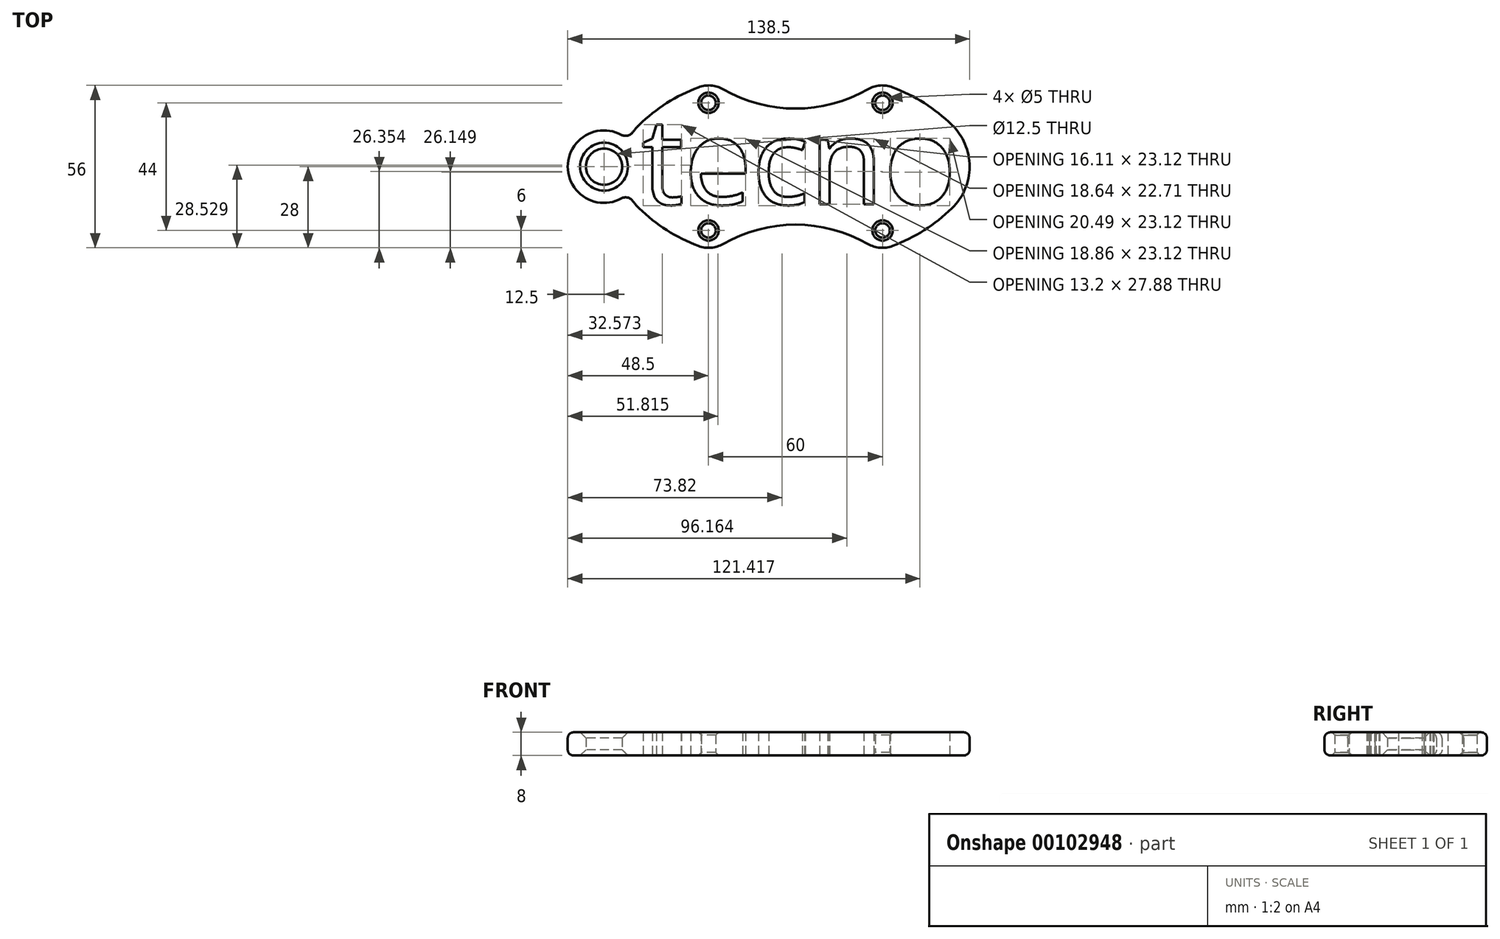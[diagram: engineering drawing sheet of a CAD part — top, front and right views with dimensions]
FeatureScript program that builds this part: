
annotation { "Feature Type Name" : "Feature", "Feature Type Description" : "" }
export const myFeature = defineFeature(function(context is Context, id is Id, definition is map)
    precondition{}
    {
        {
            var Q0;
            Q0=qCreatedBy(makeId("Top.planeOp"),FACE);
            var sketch = newSketch(context, id + "F0", { "sketchPlane" : qUnion([Q0])});
            skArc(sketch, "E0", {"start": v(-53.9, 14.37) * mm, "mid": v(-55.07, 13.14) * mm, "end": v(-56.13, 11.82) * mm});
            skArc(sketch, "E1.MirrorC", {"start": v(53.9, 14.37) * mm, "mid": v(60, 0) * mm, "end": v(53.9, -14.37) * mm});
            skArc(sketch, "E2", {"start": v(-53.9, -14.37) * mm, "mid": v(-44.35, -21.9) * mm, "end": v(-33.48, -27.35) * mm});
            skArc(sketch, "E3", {"start": v(24.94, -26.66) * mm, "mid": v(0, -20) * mm, "end": v(-24.94, -26.66) * mm});
            skArc(sketch, "E4", {"start": v(-33.48, -27.35) * mm, "mid": v(-29.13, -27.97) * mm, "end": v(-24.94, -26.66) * mm});
            skPoint(sketch, "E5.orphan", {"position": v(0, -30) * mm});
            skArc(sketch, "E6.MirrorCS", {"start": v(33.48, -27.35) * mm, "mid": v(29.13, -27.97) * mm, "end": v(24.94, -26.66) * mm});
            skArc(sketch, "E7.MirrorCS", {"start": v(53.9, -14.37) * mm, "mid": v(44.35, -21.9) * mm, "end": v(33.48, -27.35) * mm});
            skArc(sketch, "E8.MirrorCS", {"start": v(53.9, 14.37) * mm, "mid": v(44.35, 21.9) * mm, "end": v(33.48, 27.35) * mm});
            skArc(sketch, "E9.MirrorCS", {"start": v(33.48, 27.35) * mm, "mid": v(29.13, 27.97) * mm, "end": v(24.94, 26.66) * mm});
            skArc(sketch, "E10.MirrorCS", {"start": v(24.94, 26.66) * mm, "mid": v(0, 20) * mm, "end": v(-24.94, 26.66) * mm});
            skArc(sketch, "E11.MirrorCS", {"start": v(-33.48, 27.35) * mm, "mid": v(-29.13, 27.97) * mm, "end": v(-24.94, 26.66) * mm});
            skArc(sketch, "E12.MirrorCS", {"start": v(-53.9, 14.37) * mm, "mid": v(-44.35, 21.9) * mm, "end": v(-33.48, 27.35) * mm});
            skText(sketch, "E13", { "text": "tecno", "fontName": "OpenSans-Regular.ttf"});
            skArc(sketch, "E14", {"start": v(-60, 10.96) * mm, "mid": v(-78.5, 0) * mm, "end": v(-60, -10.96) * mm});
            skArc(sketch, "E15.trimOffspring", {"start": v(-56.13, -11.82) * mm, "mid": v(-55.07, -13.14) * mm, "end": v(-53.9, -14.37) * mm});
            skArc(sketch, "E16", {"start": v(-60, 10.96) * mm, "mid": v(-57.9, 10.67) * mm, "end": v(-56.13, 11.82) * mm});
            skArc(sketch, "E17.MirrorCS", {"start": v(-60, -10.96) * mm, "mid": v(-57.9, -10.67) * mm, "end": v(-56.13, -11.82) * mm});
            skCircle(sketch, "E18", {"center": v(-66, 0) * mm, "radius": 6.25 * mm});
            skCircle(sketch, "E19", {"center": v(-30, -22) * mm, "radius": 2.5 * mm});
            skCircle(sketch, "E20.MirrorC", {"center": v(-30, 22) * mm, "radius": 2.5 * mm});
            skCircle(sketch, "E21.MirrorC", {"center": v(30, 22) * mm, "radius": 2.5 * mm});
            skCircle(sketch, "E22.MirrorC", {"center": v(30, -22) * mm, "radius": 2.5 * mm});
            const initialGuessF0  = {"E13": [-0.05316, -0.013, 1, 0, 0.03]};
            skSetInitialGuess(sketch, initialGuessF0);
            skSolve(sketch);
        }
        {
            var Q0;
            Q0=makeQuery(id+"F0.imprint","IMPRINT",FACE,{"disambiguationData":[TD([[makeQuery(id+"F0.imprint","IMPRINT",EDGE,{"derivedFrom":sQuery(id+"F0.wireOp",EDGE,"E0")}),1.0]])]});
            extrude(context, id + "F1", {"entities" : qUnion([Q0]), "depth" : 8 * mm});
        }
        {
            var Q0;
            Q0=makeQuery(id+"F1.opExtrude","CAP_EDGE",EDGE,{"disambiguationData":[OSD([sQuery(id+"F0.wireOp",EDGE,"E22.MirrorC")])],"isStart":false});
            var Q1;
            Q1=makeQuery(id+"F1.opExtrude","CAP_EDGE",EDGE,{"disambiguationData":[OSD([sQuery(id+"F0.wireOp",EDGE,"E21.MirrorC")])],"isStart":false});
            var Q2;
            Q2=makeQuery(id+"F1.opExtrude","CAP_EDGE",EDGE,{"disambiguationData":[OSD([sQuery(id+"F0.wireOp",EDGE,"E20.MirrorC")])],"isStart":false});
            var Q3;
            Q3=makeQuery(id+"F1.opExtrude","CAP_EDGE",EDGE,{"disambiguationData":[OSD([sQuery(id+"F0.wireOp",EDGE,"E19")])],"isStart":false});
            var Q4;
            Q4=makeQuery(id+"F1.opExtrude","CAP_EDGE",EDGE,{"disambiguationData":[OSD([sQuery(id+"F0.wireOp",EDGE,"E19")])],"isStart":true});
            var Q5;
            Q5=makeQuery(id+"F1.opExtrude","CAP_EDGE",EDGE,{"disambiguationData":[OSD([sQuery(id+"F0.wireOp",EDGE,"E20.MirrorC")])],"isStart":true});
            var Q6;
            Q6=makeQuery(id+"F1.opExtrude","CAP_EDGE",EDGE,{"disambiguationData":[OSD([sQuery(id+"F0.wireOp",EDGE,"E22.MirrorC")])],"isStart":true});
            var Q7;
            Q7=makeQuery(id+"F1.opExtrude","CAP_EDGE",EDGE,{"disambiguationData":[OSD([sQuery(id+"F0.wireOp",EDGE,"E21.MirrorC")])],"isStart":true});
            chamfer(context, id + "F2", {"entities" : qUnion([Q0, Q1, Q2, Q3, Q4, Q5, Q6, Q7]), "width" : 1 * mm, "tangentPropagation" : true});
        }
        {
            var Q0;
            Q0=makeQuery(id+"F1.opExtrude","CAP_EDGE",EDGE,{"disambiguationData":[OSD([sQuery(id+"F0.wireOp",EDGE,"E18")])],"isStart":false});
            var Q1;
            Q1=makeQuery(id+"F1.opExtrude","CAP_EDGE",EDGE,{"disambiguationData":[OSD([sQuery(id+"F0.wireOp",EDGE,"E18")])],"isStart":true});
            chamfer(context, id + "F3", {"entities" : qUnion([Q0, Q1]), "width" : 2 * mm, "tangentPropagation" : true});
        }
        {
            var Q0;
            Q0=makeQuery(id+"F1.opExtrude","CAP_EDGE",EDGE,{"disambiguationData":[OSD([sQuery(id+"F0.wireOp",EDGE,"E3")])],"isStart":false});
            var Q1;
            Q1=makeQuery(id+"F1.opExtrude","CAP_EDGE",EDGE,{"disambiguationData":[OSD([sQuery(id+"F0.wireOp",EDGE,"E7.MirrorCS")])],"isStart":true});
            fillet(context, id + "F4", {"entities" : qUnion([Q0, Q1]), "radius" : 2 * mm, "tangentPropagation" : true, "allowEdgeOverflow" : false});
        }
    });
